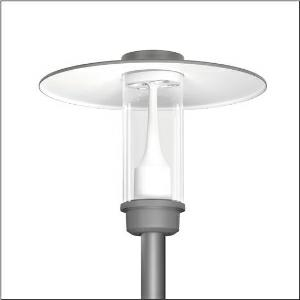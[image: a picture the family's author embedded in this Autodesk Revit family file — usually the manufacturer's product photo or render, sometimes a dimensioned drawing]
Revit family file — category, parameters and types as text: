
# Revit family: litepole_2_iq___p1_0a_5xa5425ff14h000022_e316
name_source: partatom
category: Lighting Fixtures
units: mm (PartAtom-declared; Revit-internal decimal feet)

## family parameters
Cut with Voids When Loaded = No
Host = Face
Light Source = No
Part Type = Normal
Room Calculation Point = No
Round Connector Dimension = Use Diameter
Shared = No

## types (1)
- --- (1 x LED, 1520 lm, 10.5 W, 3000K)
    Apparent Load = 11 VA
    CIE Flux Codes = 33 62 89 96 100
    Color Rendering = 70
    Color Temperature = 3000K
    Default Elevation = 1800 mm
    Description = Litepole 2 iQ, mast luminaire, Module 540 iQ-SR, primary light control with 3 zone facetted reflector, of plastic, silver coated, highly specular, structured, primary optical cover: cover, of PMMA, transparent, light distribution: P1.0a, light emission: direct distribution, primary light characteristic: strongly asymmetric, installation type: post-top, LED, High Power LED, rated luminous flux: 1.520lm, luminous efficacy: 145lm/W, light colour: 730, colour temperature: 3000K, control gear: iQ Street-Remote, control: Street-Remote, Auto-Match, Temp-Guard, Lumen-Switch, Night-Set, Smart-Wire, Light-Fading, Desk-Remote (wireless, voltage-free reading and setting of iQ features in the workshop via application-optimized NFC function/RFID function), optimised constant luminous flux control (CLO 2.0), pre-setting: logarithmic dimming characteristic, mains connection: 230..240V, AC, 50/60Hz, connection cable pre-assembled, cable length: 5,5m, wiring characteristics: H07RN-F, start of lifetime: 11W, end of service life: 11W, reduction: 5W, luminaire housing, upper part, of aluminium, coated, SITECO metallic grey (DB 702S), diameter: 750mm, height: 590mm, spigot size: d x l = 76 x 70mm (post-top) | with reducer (optional accessory) 60 x 70mm, mounting height: 3..5m, post-top mast mounting element, of diecast aluminium, coated, SITECO metallic grey (DB 702S), Module 540 iQ-SR, traffic white (RAL 9016), equipment: standard, protection rating (complete): IP65, insulation class (complete): insulation class II (safety insulation), certification: CE, ENEC, VDE, packaging unit: 1 piece

Light Distribution: P1.0a
    Height = 590 mm
    Lamp = 1 x LED
    Lamp Light Flux = 1520 lm
    Lamp Power = 10.5 W
    Lamp count = 1
    Length = 750 mm
    Luminous efficacy = 145 lm/W
    Manufacturer = Siteco
    ModVariant = No
    Model = 5XA5425FF14H000022
    Number of Poles = 1
    OnlyDefault = Yes
    Power Factor = 1
    Product Name = Litepole 2 iQ | P1.0a
    Product group = mast luminaire | pylon top
    ProductGroupID = 6100
    Protection Class = Protection class II
    Protection Degree = IP 65
    RLX_Detail_Level = 1
    RLX_Emergency_Light_Flux = 0 lm
    RLX_Emergency_Type = 0
    RLX_Emergency_Type_DB = No
    RlxData = <blob elided: 31109 chars, md5=54826ddb>
    Socket = socket
    Standby Power = 0 W
    System Light Flux = 1520 lm
    System Power = 11 W
    Type Comments = factory setting: luminous flux: 100 % | dim-lin: 254 | 419 mA
    Type Image = l_1006518.jpg
    URL = http://relux.com
    VarID = @adj_189913
    Voltage = 0 V
    Weight = 0.00 kg
    Width = 0 mm  [stored 0 ft]

note: [stored X ft] marks values corroborated as IEEE doubles in the binary element streams (Revit-internal decimal feet)

## geometry (parser evidence)
native form markers: Blend x4, Sweep x8
no freeform markers — native parametric forms only
